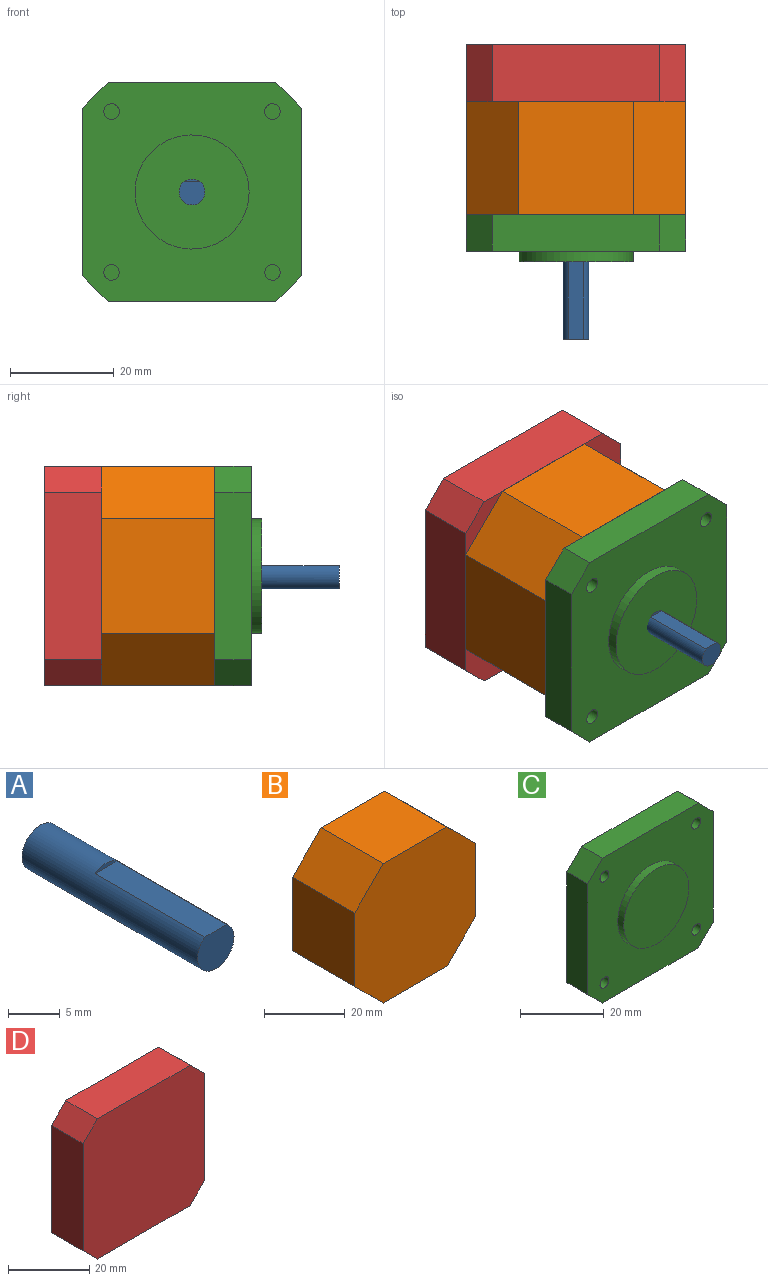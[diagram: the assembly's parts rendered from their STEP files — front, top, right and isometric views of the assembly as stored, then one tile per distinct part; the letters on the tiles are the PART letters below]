
ASSEMBLY  parts=4 mates=3
PART A: 5 faces, bbox 5x24x5 mm
  f0: cylinder r=2.5mm len=24mm, axis (0,1,0), area 328.7mm2, adj f1,f2,f3,f4
  f1: plane 5x4.5mm, normal (0,-1,0), area 18.6mm2, adj f0,f3
  f2: plane 5x5mm, normal (0,1,0), area 19.6mm2, adj f0
  f3: plane 15x3mm, normal (0,0,1), area 45mm2, adj f0,f1,f4
  f4: plane 3x0.5mm, normal (0,-1,0), area 1mm2, adj f0,f3
PART B: 10 faces, bbox 42.3x21.8x42.3 mm
  f0: plane 21.8x10mm, normal (0.71,0,0.71), area 308.3mm2, adj f3,f6,f7,f8
  f1: plane 21.8x10mm, normal (0.71,0,-0.71), area 308.3mm2, adj f3,f4,f6,f7
  f2: plane 21.8x10mm, normal (-0.71,0,0.71), area 308.3mm2, adj f6,f7,f8,f9
  f3: plane 22.3x21.8mm, normal (1,0,0), area 486.1mm2, adj f0,f1,f6,f7
  f4: plane 22.3x21.8mm, normal (0,0,-1), area 486.1mm2, adj f1,f5,f6,f7
  f5: plane 21.8x10mm, normal (-0.71,0,-0.71), area 308.3mm2, adj f4,f6,f7,f9
  f6: plane 42.3x42.3mm, normal (0,-1,0), area 1589.3mm2, adj f0,f1,f2,f3,f4,f5,f8,f9
  f7: plane 42.3x42.3mm, normal (0,1,0), area 1589.3mm2, adj f0,f1,f2,f3,f4,f5,f8,f9
  f8: plane 22.3x21.8mm, normal (0,0,1), area 486.1mm2, adj f0,f2,f6,f7
  f9: plane 22.3x21.8mm, normal (-1,0,0), area 486.1mm2, adj f2,f5,f6,f7
PART C: 20 faces, bbox 42.3x9x42.3 mm
  f0: plane 42.3x42.3mm, normal (0,-1,0), area 1330.9mm2, adj f1,f2,f3,f4,f6,f7,f8,f9
  f1: plane 32.3x7mm, normal (-1,0,0), area 226.1mm2, adj f0,f5,f6,f9
  f2: plane 32.3x7mm, normal (0,0,-1), area 226.1mm2, adj f0,f5,f6,f7
  f3: plane 32.3x7mm, normal (1,0,0), area 226.1mm2, adj f0,f5,f7,f8
  f4: plane 32.3x7mm, normal (0,0,1), area 226.1mm2, adj f0,f5,f8,f9
  f5: plane 42.3x42.3mm, normal (0,1,0), area 1739.3mm2, adj f1,f2,f3,f4,f6,f7,f8,f9
  f6: plane 7x5mm, normal (-0.71,0,-0.71), area 49.5mm2, adj f0,f1,f2,f5
  f7: plane 7x5mm, normal (0.71,0,-0.71), area 49.5mm2, adj f0,f2,f3,f5
  f8: plane 7x5mm, normal (0.71,0,0.71), area 49.5mm2, adj f0,f3,f4,f5
  f9: plane 7x5mm, normal (-0.71,0,0.71), area 49.5mm2, adj f0,f1,f4,f5
  f10: cylinder r=11mm len=22mm, axis (0,1,0), area 138.2mm2, adj f0,f11
  f11: plane 22x22mm, normal (0,-1,0), area 380.1mm2, adj f10
  f12: cylinder r=1.5mm len=4.5mm, axis (0,-1,0), area 42.4mm2, adj f0,f13
  f13: plane 3x3mm, normal (0,-1,0), area 7.1mm2, adj f12
  f14: cylinder r=1.5mm len=4.5mm, axis (0,-1,0), area 42.4mm2, adj f0,f15
  f15: plane 3x3mm, normal (0,-1,0), area 7.1mm2, adj f14
  f16: cylinder r=1.5mm len=4.5mm, axis (0,-1,0), area 42.4mm2, adj f0,f17
  f17: plane 3x3mm, normal (0,-1,0), area 7.1mm2, adj f16
  f18: cylinder r=1.5mm len=4.5mm, axis (0,-1,0), area 42.4mm2, adj f0,f19
  f19: plane 3x3mm, normal (0,-1,0), area 7.1mm2, adj f18
PART D: 18 faces, bbox 42.3x11x42.3 mm
  f0: plane 32.3x11mm, normal (1,0,0), area 355.3mm2, adj f4,f5,f8,f9
  f1: plane 32.3x11mm, normal (0,0,-1), area 355.3mm2, adj f4,f5,f7,f8
  f2: plane 32.3x11mm, normal (-1,0,0), area 355.3mm2, adj f4,f5,f6,f7
  f3: plane 32.3x11mm, normal (0,0,1), area 355.3mm2, adj f4,f5,f6,f9
  f4: plane 42.3x42.3mm, normal (0,1,0), area 1711mm2, adj f0,f1,f2,f3,f6,f7,f8,f9
  f5: plane 42.3x42.3mm, normal (0,-1,0), area 1739.3mm2, adj f0,f1,f2,f3,f6,f7,f8,f9
  f6: plane 11x5mm, normal (-0.71,0,0.71), area 77.8mm2, adj f2,f3,f4,f5
  f7: plane 11x5mm, normal (-0.71,0,-0.71), area 77.8mm2, adj f1,f2,f4,f5
  f8: plane 11x5mm, normal (0.71,0,-0.71), area 77.8mm2, adj f0,f1,f4,f5
  f9: plane 11x5mm, normal (0.71,0,0.71), area 77.8mm2, adj f0,f3,f4,f5
  f10: cylinder r=1.5mm len=4.5mm, axis (0,1,0), area 42.4mm2, adj f4,f11
  f11: plane 3x3mm, normal (0,1,0), area 7.1mm2, adj f10
  f12: cylinder r=1.5mm len=4.5mm, axis (0,1,0), area 42.4mm2, adj f4,f13
  f13: plane 3x3mm, normal (0,1,0), area 7.1mm2, adj f12
  f14: cylinder r=1.5mm len=4.5mm, axis (0,1,0), area 42.4mm2, adj f4,f15
  f15: plane 3x3mm, normal (0,1,0), area 7.1mm2, adj f14
  f16: cylinder r=1.5mm len=4.5mm, axis (0,1,0), area 42.4mm2, adj f4,f17
  f17: plane 3x3mm, normal (0,1,0), area 7.1mm2, adj f16
PLACE A t=(4.18,-9.14,12.66)mm
PLACE B t=(4.18,-18.14,12.66)mm
PLACE C t=(4.18,-18.14,12.66)mm
PLACE D t=(4.18,-18.14,12.66)mm
MATE fastened C.f10 <-> B.f6  axis (0,1,0) through (-14.27,-18.14,26.09)mm
MATE fastened A.f0 <-> B.f6  axis (0,1,0) through (-14.27,-18.14,26.09)mm
MATE fastened B.f7 <-> D.f5  axis (0,1,0) through (-14.27,3.66,26.09)mm
